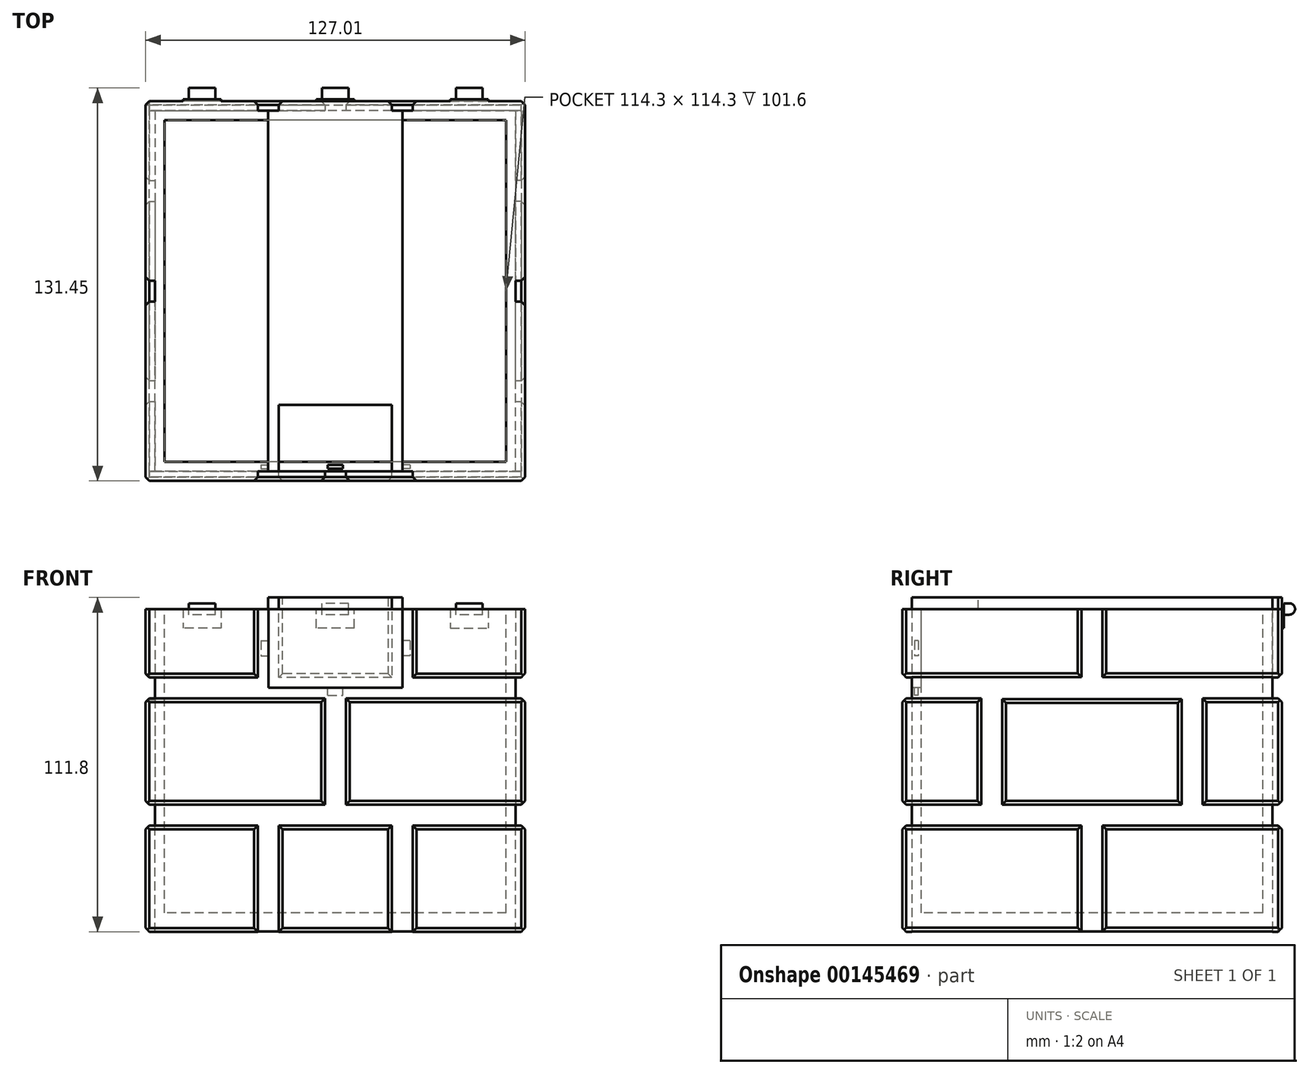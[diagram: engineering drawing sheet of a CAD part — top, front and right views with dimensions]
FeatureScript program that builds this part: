
annotation { "Feature Type Name" : "Feature", "Feature Type Description" : "" }
export const myFeature = defineFeature(function(context is Context, id is Id, definition is map)
    precondition{}
    {
        {
            var Q0;
            Q0=qCreatedBy(makeId("Front.planeOp"),FACE);
            var sketch = newSketch(context, id + "F0", { "sketchPlane" : qUnion([Q0])});
            skLineSegment(sketch, "E0.bottom", {"start": v(60.33, 60.32) * mm, "end": v(-60.33, 60.32) * mm});
            skLineSegment(sketch, "E0.top", {"start": v(60.33, -60.33) * mm, "end": v(-60.33, -60.33) * mm});
            skLineSegment(sketch, "E0.left", {"start": v(60.33, 60.32) * mm, "end": v(60.33, -60.33) * mm});
            skLineSegment(sketch, "E0.right", {"start": v(-60.32, 60.32) * mm, "end": v(-60.33, -60.33) * mm});
            skPoint(sketch, "E0.middle", {"position": v(0, 0) * mm});
            skSolve(sketch);
        }
        {
            var Q0;
            Q0=makeQuery(id+"F0.imprint","IMPRINT",FACE,{"disambiguationData":[TD([[makeQuery(id+"F0.imprint","IMPRINT",EDGE,{"derivedFrom":sQuery(id+"F0.wireOp",EDGE,"E0.bottom")}),1.0]])]});
            extrude(context, id + "F1", {"entities" : qUnion([Q0]), "depth" : 60.32 * mm, "hasSecondDirection" : true, "secondDirectionOppositeDirection" : true, "secondDirectionDepth" : 60.32 * mm});
        }
        {
            var Q0;
            Q0=makeQuery(id+"F1.opExtrude","CAP_FACE",FACE,{"disambiguationData":[OSD([sQuery(id+"F0.wireOp",EDGE,"E0.bottom"),sQuery(id+"F0.wireOp",EDGE,"E0.top"),sQuery(id+"F0.wireOp",EDGE,"E0.left"),sQuery(id+"F0.wireOp",EDGE,"E0.right")])],"isStart":false});
            var sketch = newSketch(context, id + "F2", { "sketchPlane" : qUnion([Q0])});
            skLineSegment(sketch, "E1", {"start": v(-63.5, -60.36) * mm, "end": v(-63.5, -24.8) * mm});
            skLineSegment(sketch, "E2", {"start": v(-63.5, -24.8) * mm, "end": v(-25.9, -24.8) * mm});
            skLineSegment(sketch, "E3", {"start": v(-25.9, -24.8) * mm, "end": v(-25.9, -60.36) * mm});
            skLineSegment(sketch, "E4", {"start": v(-25.9, -60.36) * mm, "end": v(-63.5, -60.36) * mm});
            skLineSegment(sketch, "E5", {"start": v(-63.5, 17.75) * mm, "end": v(-3.49, 17.75) * mm});
            skLineSegment(sketch, "E6", {"start": v(-3.49, 17.75) * mm, "end": v(-3.49, -17.81) * mm});
            skLineSegment(sketch, "E7", {"start": v(-3.49, -17.81) * mm, "end": v(-63.5, -17.81) * mm});
            skLineSegment(sketch, "E8", {"start": v(-63.5, -17.81) * mm, "end": v(-63.5, 17.75) * mm});
            skLineSegment(sketch, "E9", {"start": v(3.5, 17.75) * mm, "end": v(3.5, -17.81) * mm});
            skLineSegment(sketch, "E10", {"start": v(3.5, -17.81) * mm, "end": v(63.5, -17.81) * mm});
            skLineSegment(sketch, "E11", {"start": v(63.5, -17.81) * mm, "end": v(63.5, 17.75) * mm});
            skLineSegment(sketch, "E12", {"start": v(63.5, 17.75) * mm, "end": v(3.5, 17.75) * mm});
            skLineSegment(sketch, "E13", {"start": v(-18.92, -60.36) * mm, "end": v(-18.92, -24.8) * mm});
            skLineSegment(sketch, "E14", {"start": v(-18.92, -24.8) * mm, "end": v(18.93, -24.8) * mm});
            skLineSegment(sketch, "E15", {"start": v(18.93, -24.8) * mm, "end": v(18.93, -60.36) * mm});
            skLineSegment(sketch, "E16", {"start": v(18.93, -60.36) * mm, "end": v(-18.92, -60.36) * mm});
            skLineSegment(sketch, "E17", {"start": v(25.91, -60.36) * mm, "end": v(25.91, -24.8) * mm});
            skLineSegment(sketch, "E18", {"start": v(25.91, -24.8) * mm, "end": v(63.5, -24.8) * mm});
            skLineSegment(sketch, "E19", {"start": v(63.5, -24.8) * mm, "end": v(63.5, -60.36) * mm});
            skLineSegment(sketch, "E20", {"start": v(63.5, -60.36) * mm, "end": v(25.91, -60.36) * mm});
            skLineSegment(sketch, "E21.MirrorCS", {"start": v(-63.5, 24.73) * mm, "end": v(-25.9, 24.73) * mm});
            skLineSegment(sketch, "E22.MirrorCS", {"start": v(-25.9, 24.73) * mm, "end": v(-25.9, 60.3) * mm});
            skLineSegment(sketch, "E23.MirrorCS", {"start": v(-25.9, 60.3) * mm, "end": v(-63.5, 60.3) * mm});
            skLineSegment(sketch, "E24.MirrorCS", {"start": v(-63.5, 60.3) * mm, "end": v(-63.5, 24.73) * mm});
            skLineSegment(sketch, "E25.MirrorCS", {"start": v(-18.92, 24.73) * mm, "end": v(18.93, 24.73) * mm});
            skLineSegment(sketch, "E26.MirrorCS", {"start": v(-18.92, 60.3) * mm, "end": v(-18.92, 24.73) * mm});
            skLineSegment(sketch, "E27.MirrorCS", {"start": v(18.93, 60.3) * mm, "end": v(-18.92, 60.3) * mm});
            skLineSegment(sketch, "E28.MirrorCS", {"start": v(18.93, 24.73) * mm, "end": v(18.93, 60.3) * mm});
            skLineSegment(sketch, "E29.MirrorCS", {"start": v(25.91, 24.73) * mm, "end": v(63.5, 24.73) * mm});
            skLineSegment(sketch, "E30.MirrorCS", {"start": v(25.91, 60.3) * mm, "end": v(25.91, 24.73) * mm});
            skLineSegment(sketch, "E31.MirrorCS", {"start": v(63.5, 60.3) * mm, "end": v(25.91, 60.3) * mm});
            skLineSegment(sketch, "E32.MirrorCS", {"start": v(63.5, 24.73) * mm, "end": v(63.5, 60.3) * mm});
            skLineSegment(sketch, "E33", {"start": v(-60.32, 24.73) * mm, "end": v(-60.32, 17.75) * mm});
            skSolve(sketch);
        }
        {
            var Q0;
            Q0 = qSketchRegion(id + "F2", true);
            extrude(context, id + "F3", {"entities" : qUnion([Q0]), "operationType" : NewBodyOperationType.ADD, "depth" : 3.17 * mm});
        }
        {
            var Q0;
            Q0=makeQuery(id+"F1.opExtrude","CAP_FACE",FACE,{"disambiguationData":[OSD([sQuery(id+"F0.wireOp",EDGE,"E0.bottom"),sQuery(id+"F0.wireOp",EDGE,"E0.top"),sQuery(id+"F0.wireOp",EDGE,"E0.left"),sQuery(id+"F0.wireOp",EDGE,"E0.right")])],"isStart":true});
            var sketch = newSketch(context, id + "F4", { "sketchPlane" : qUnion([Q0])});
            skLineSegment(sketch, "E34", {"start": v(-63.5, -60.36) * mm, "end": v(-63.5, -24.8) * mm});
            skLineSegment(sketch, "E35", {"start": v(-63.5, -24.8) * mm, "end": v(-25.91, -24.8) * mm});
            skLineSegment(sketch, "E36", {"start": v(-25.91, -24.8) * mm, "end": v(-25.91, -60.36) * mm});
            skLineSegment(sketch, "E37", {"start": v(-25.91, -60.36) * mm, "end": v(-63.5, -60.36) * mm});
            skLineSegment(sketch, "E38", {"start": v(-63.5, 17.75) * mm, "end": v(-3.5, 17.75) * mm});
            skLineSegment(sketch, "E39", {"start": v(-3.5, 17.75) * mm, "end": v(-3.5, -17.81) * mm});
            skLineSegment(sketch, "E40", {"start": v(-3.5, -17.81) * mm, "end": v(-63.5, -17.81) * mm});
            skLineSegment(sketch, "E41", {"start": v(-63.5, -17.81) * mm, "end": v(-63.5, 17.75) * mm});
            skLineSegment(sketch, "E42", {"start": v(3.49, 17.75) * mm, "end": v(3.49, -17.81) * mm});
            skLineSegment(sketch, "E43", {"start": v(3.49, -17.81) * mm, "end": v(63.5, -17.81) * mm});
            skLineSegment(sketch, "E44", {"start": v(63.5, -17.81) * mm, "end": v(63.5, 17.75) * mm});
            skLineSegment(sketch, "E45", {"start": v(63.5, 17.75) * mm, "end": v(3.49, 17.75) * mm});
            skLineSegment(sketch, "E46", {"start": v(-18.93, -60.36) * mm, "end": v(-18.93, -24.8) * mm});
            skLineSegment(sketch, "E47", {"start": v(-18.93, -24.8) * mm, "end": v(18.92, -24.8) * mm});
            skLineSegment(sketch, "E48", {"start": v(18.92, -24.8) * mm, "end": v(18.92, -60.36) * mm});
            skLineSegment(sketch, "E49", {"start": v(18.92, -60.36) * mm, "end": v(-18.93, -60.36) * mm});
            skLineSegment(sketch, "E50", {"start": v(25.9, -60.36) * mm, "end": v(25.9, -24.8) * mm});
            skLineSegment(sketch, "E51", {"start": v(25.9, -24.8) * mm, "end": v(63.5, -24.8) * mm});
            skLineSegment(sketch, "E52", {"start": v(63.5, -24.8) * mm, "end": v(63.5, -60.36) * mm});
            skLineSegment(sketch, "E53", {"start": v(63.5, -60.36) * mm, "end": v(25.9, -60.36) * mm});
            skLineSegment(sketch, "E54.MirrorCS", {"start": v(-63.5, 24.73) * mm, "end": v(-25.91, 24.73) * mm});
            skLineSegment(sketch, "E55.MirrorCS", {"start": v(-25.91, 24.73) * mm, "end": v(-25.91, 60.3) * mm});
            skLineSegment(sketch, "E56.MirrorCS", {"start": v(-25.91, 60.3) * mm, "end": v(-63.5, 60.3) * mm});
            skLineSegment(sketch, "E57.MirrorCS", {"start": v(-63.5, 60.3) * mm, "end": v(-63.5, 24.73) * mm});
            skLineSegment(sketch, "E58.MirrorCS", {"start": v(-18.93, 24.73) * mm, "end": v(18.92, 24.73) * mm});
            skLineSegment(sketch, "E59.MirrorCS", {"start": v(-18.93, 60.3) * mm, "end": v(-18.93, 24.73) * mm});
            skLineSegment(sketch, "E60.MirrorCS", {"start": v(18.92, 60.3) * mm, "end": v(-18.93, 60.3) * mm});
            skLineSegment(sketch, "E61.MirrorCS", {"start": v(18.92, 24.73) * mm, "end": v(18.92, 60.3) * mm});
            skLineSegment(sketch, "E62.MirrorCS", {"start": v(25.9, 24.73) * mm, "end": v(63.5, 24.73) * mm});
            skLineSegment(sketch, "E63.MirrorCS", {"start": v(25.9, 60.3) * mm, "end": v(25.9, 24.73) * mm});
            skLineSegment(sketch, "E64.MirrorCS", {"start": v(63.5, 60.3) * mm, "end": v(25.9, 60.3) * mm});
            skLineSegment(sketch, "E65.MirrorCS", {"start": v(63.5, 24.73) * mm, "end": v(63.5, 60.3) * mm});
            skLineSegment(sketch, "E66", {"start": v(-60.33, 24.73) * mm, "end": v(-60.33, 17.75) * mm});
            skSolve(sketch);
        }
        {
            var Q0;
            {var subQ0=sQuery(id+"F4.wireOp",EDGE,"E55.MirrorCS");Q0=makeQuery(id+"F4.imprint","IMPRINT",FACE,{"disambiguationData":[TD([[makeQuery(id+"F4.imprint","IMPRINT",EDGE,{"derivedFrom":subQ0}),1.0]])]});}
            var Q1;
            Q1=makeQuery(id+"F4.imprint","IMPRINT",FACE,{"disambiguationData":[TD([[makeQuery(id+"F4.imprint","IMPRINT",EDGE,{"derivedFrom":sQuery(id+"F4.wireOp",EDGE,"E59.MirrorCS")}),1.0]])]});
            var Q2;
            {var subQ0=sQuery(id+"F4.wireOp",EDGE,"E39");Q2=makeQuery(id+"F4.imprint","IMPRINT",FACE,{"disambiguationData":[TD([[makeQuery(id+"F4.imprint","IMPRINT",EDGE,{"derivedFrom":subQ0}),-1.0]])]});}
            var Q3;
            {var subQ0=sQuery(id+"F4.wireOp",EDGE,"E41");Q3=makeQuery(id+"F4.imprint","IMPRINT",FACE,{"disambiguationData":[TD([[makeQuery(id+"F4.imprint","IMPRINT",EDGE,{"derivedFrom":subQ0}),-1.0]])]});}
            var Q4;
            {var subQ0=sQuery(id+"F4.wireOp",EDGE,"E57.MirrorCS");Q4=makeQuery(id+"F4.imprint","IMPRINT",FACE,{"disambiguationData":[TD([[makeQuery(id+"F4.imprint","IMPRINT",EDGE,{"derivedFrom":subQ0}),1.0]])]});}
            var Q5;
            {var subQ0=sQuery(id+"F4.wireOp",EDGE,"E63.MirrorCS");Q5=makeQuery(id+"F4.imprint","IMPRINT",FACE,{"disambiguationData":[TD([[makeQuery(id+"F4.imprint","IMPRINT",EDGE,{"derivedFrom":subQ0}),1.0]])]});}
            var Q6;
            {var subQ0=sQuery(id+"F4.wireOp",EDGE,"E65.MirrorCS");Q6=makeQuery(id+"F4.imprint","IMPRINT",FACE,{"disambiguationData":[TD([[makeQuery(id+"F4.imprint","IMPRINT",EDGE,{"derivedFrom":subQ0}),1.0]])]});}
            var Q7;
            {var subQ0=sQuery(id+"F4.wireOp",EDGE,"E42");Q7=makeQuery(id+"F4.imprint","IMPRINT",FACE,{"disambiguationData":[TD([[makeQuery(id+"F4.imprint","IMPRINT",EDGE,{"derivedFrom":subQ0}),1.0]])]});}
            var Q8;
            {var subQ0=sQuery(id+"F4.wireOp",EDGE,"E44");Q8=makeQuery(id+"F4.imprint","IMPRINT",FACE,{"disambiguationData":[TD([[makeQuery(id+"F4.imprint","IMPRINT",EDGE,{"derivedFrom":subQ0}),1.0]])]});}
            var Q9;
            {var subQ6=sQuery(id+"F4.wireOp",EDGE,"E52");Q9=makeQuery(id+"F4.imprint","IMPRINT",FACE,{"disambiguationData":[TD([[makeQuery(id+"F4.imprint","IMPRINT",EDGE,{"derivedFrom":subQ6}),-1.0]])]});}
            var Q10;
            {var subQ0=sQuery(id+"F4.wireOp",EDGE,"E51");var subQ1=sQuery(id+"F4.wireOp",EDGE,"E50");var subQ2=makeQuery(id+"F4.imprint","INTERSECT",VERTEX,{"derivedFrom":[subQ1,subQ0]});Q10=makeQuery(id+"F4.imprint","IMPRINT",FACE,{"disambiguationData":[TD([[makeQuery(id+"F4.imprint","IMPRINT",EDGE,{"disambiguationData":[TD([[subQ2,1.0]])],"derivedFrom":subQ1}),-1.0]])]});}
            var Q11;
            {var subQ0=sQuery(id+"F4.wireOp",EDGE,"E47");Q11=makeQuery(id+"F4.imprint","IMPRINT",FACE,{"disambiguationData":[TD([[makeQuery(id+"F4.imprint","IMPRINT",EDGE,{"derivedFrom":subQ0}),-1.0]])]});}
            var Q12;
            {var subQ0=sQuery(id+"F4.wireOp",EDGE,"E36");var subQ1=sQuery(id+"F4.wireOp",EDGE,"E35");var subQ2=makeQuery(id+"F4.imprint","INTERSECT",VERTEX,{"derivedFrom":[subQ1,subQ0]});Q12=makeQuery(id+"F4.imprint","IMPRINT",FACE,{"disambiguationData":[TD([[makeQuery(id+"F4.imprint","IMPRINT",EDGE,{"disambiguationData":[TD([[subQ2,1.0]])],"derivedFrom":subQ1}),-1.0]])]});}
            var Q13;
            {var subQ2=sQuery(id+"F4.wireOp",EDGE,"E34");Q13=makeQuery(id+"F4.imprint","IMPRINT",FACE,{"disambiguationData":[TD([[makeQuery(id+"F4.imprint","IMPRINT",EDGE,{"derivedFrom":subQ2}),-1.0]])]});}
            extrude(context, id + "F5", {"entities" : qUnion([Q0, Q1, Q2, Q3, Q4, Q5, Q6, Q7, Q8, Q9, Q10, Q11, Q12, Q13]), "operationType" : NewBodyOperationType.ADD, "depth" : 3.17 * mm});
        }
        {
            var Q0;
            Q0=makeQuery(id+"F1.opExtrude","SWEPT_FACE",FACE,{"disambiguationData":[OSD([sQuery(id+"F0.wireOp",EDGE,"E0.left")])]});
            var sketch = newSketch(context, id + "F6", { "sketchPlane" : qUnion([Q0])});
            skLineSegment(sketch, "E67.bottom", {"start": v(-63.5, 60.33) * mm, "end": v(-3.5, 60.33) * mm});
            skLineSegment(sketch, "E67.top", {"start": v(-63.5, 24.77) * mm, "end": v(-3.5, 24.77) * mm});
            skLineSegment(sketch, "E67.left", {"start": v(-63.5, 60.33) * mm, "end": v(-63.5, 24.77) * mm});
            skLineSegment(sketch, "E67.right", {"start": v(-3.5, 60.33) * mm, "end": v(-3.5, 24.77) * mm});
            skLineSegment(sketch, "E68.bottom", {"start": v(63.5, 60.33) * mm, "end": v(3.5, 60.33) * mm});
            skLineSegment(sketch, "E68.top", {"start": v(63.5, 24.76) * mm, "end": v(3.5, 24.76) * mm});
            skLineSegment(sketch, "E68.left", {"start": v(63.5, 60.33) * mm, "end": v(63.5, 24.76) * mm});
            skLineSegment(sketch, "E68.right", {"start": v(3.5, 60.33) * mm, "end": v(3.5, 24.76) * mm});
            skLineSegment(sketch, "E69.bottom", {"start": v(-63.5, 17.75) * mm, "end": v(-37, 17.75) * mm});
            skLineSegment(sketch, "E69.top", {"start": v(-63.5, -17.81) * mm, "end": v(-37, -17.81) * mm});
            skLineSegment(sketch, "E69.left", {"start": v(-63.5, 17.75) * mm, "end": v(-63.5, -17.81) * mm});
            skLineSegment(sketch, "E69.right", {"start": v(-37, 17.75) * mm, "end": v(-37, -17.81) * mm});
            skLineSegment(sketch, "E70.bottom", {"start": v(-30.01, 17.38) * mm, "end": v(30, 17.38) * mm});
            skLineSegment(sketch, "E70.top", {"start": v(-30.01, -17.81) * mm, "end": v(30, -17.81) * mm});
            skLineSegment(sketch, "E70.left", {"start": v(-30.01, 17.38) * mm, "end": v(-30.01, -17.81) * mm});
            skLineSegment(sketch, "E70.right", {"start": v(30, 17.38) * mm, "end": v(30, -17.81) * mm});
            skLineSegment(sketch, "E71.bottom", {"start": v(36.98, 17.75) * mm, "end": v(63.49, 17.75) * mm});
            skLineSegment(sketch, "E71.top", {"start": v(36.98, -17.81) * mm, "end": v(63.49, -17.81) * mm});
            skLineSegment(sketch, "E71.left", {"start": v(36.98, 17.75) * mm, "end": v(36.98, -17.81) * mm});
            skLineSegment(sketch, "E71.right", {"start": v(63.49, 17.75) * mm, "end": v(63.49, -17.81) * mm});
            skLineSegment(sketch, "E72.bottom", {"start": v(-63.5, -60.33) * mm, "end": v(-3.5, -60.33) * mm});
            skLineSegment(sketch, "E72.top", {"start": v(-63.5, -24.8) * mm, "end": v(-3.5, -24.8) * mm});
            skLineSegment(sketch, "E72.left", {"start": v(-63.5, -60.33) * mm, "end": v(-63.5, -24.8) * mm});
            skLineSegment(sketch, "E72.right", {"start": v(-3.5, -60.33) * mm, "end": v(-3.5, -24.8) * mm});
            skLineSegment(sketch, "E73.bottom", {"start": v(63.5, -60.33) * mm, "end": v(3.5, -60.33) * mm});
            skLineSegment(sketch, "E73.top", {"start": v(63.5, -24.8) * mm, "end": v(3.5, -24.8) * mm});
            skLineSegment(sketch, "E73.left", {"start": v(63.5, -60.33) * mm, "end": v(63.5, -24.8) * mm});
            skLineSegment(sketch, "E73.right", {"start": v(3.5, -60.33) * mm, "end": v(3.5, -24.8) * mm});
            skSolve(sketch);
        }
        {
            var Q0;
            {var subQ10=sQuery(id+"F6.wireOp",EDGE,"E68.right");Q0=makeQuery(id+"F6.imprint","IMPRINT",FACE,{"disambiguationData":[TD([[makeQuery(id+"F6.imprint","IMPRINT",EDGE,{"derivedFrom":subQ10}),1.0]])]});}
            var Q1;
            Q1=makeQuery(id+"F6.imprint","IMPRINT",FACE,{"disambiguationData":[TD([[makeQuery(id+"F6.imprint","IMPRINT",EDGE,{"derivedFrom":sQuery(id+"F6.wireOp",EDGE,"E70.bottom")}),-1.0]])]});
            var Q2;
            {var subQ14=sQuery(id+"F6.wireOp",EDGE,"E71.left");Q2=makeQuery(id+"F6.imprint","IMPRINT",FACE,{"disambiguationData":[TD([[makeQuery(id+"F6.imprint","IMPRINT",EDGE,{"derivedFrom":subQ14}),1.0]])]});}
            var Q3;
            {var subQ12=sQuery(id+"F6.wireOp",EDGE,"E69.right");Q3=makeQuery(id+"F6.imprint","IMPRINT",FACE,{"disambiguationData":[TD([[makeQuery(id+"F6.imprint","IMPRINT",EDGE,{"derivedFrom":subQ12}),-1.0]])]});}
            var Q4;
            {var subQ10=sQuery(id+"F6.wireOp",EDGE,"E72.right");Q4=makeQuery(id+"F6.imprint","IMPRINT",FACE,{"disambiguationData":[TD([[makeQuery(id+"F6.imprint","IMPRINT",EDGE,{"derivedFrom":subQ10}),1.0]])]});}
            var Q5;
            {var subQ6=sQuery(id+"F6.wireOp",EDGE,"E73.right");Q5=makeQuery(id+"F6.imprint","IMPRINT",FACE,{"disambiguationData":[TD([[makeQuery(id+"F6.imprint","IMPRINT",EDGE,{"derivedFrom":subQ6}),-1.0]])]});}
            var Q6;
            {var subQ10=sQuery(id+"F6.wireOp",EDGE,"E67.right");Q6=makeQuery(id+"F6.imprint","IMPRINT",FACE,{"disambiguationData":[TD([[makeQuery(id+"F6.imprint","IMPRINT",EDGE,{"derivedFrom":subQ10}),-1.0]])]});}
            extrude(context, id + "F7", {"entities" : qUnion([Q0, Q1, Q2, Q3, Q4, Q5, Q6]), "operationType" : NewBodyOperationType.ADD, "depth" : 3.17 * mm});
        }
        {
            var Q0;
            Q0=makeQuery(id+"F1.opExtrude","SWEPT_FACE",FACE,{"disambiguationData":[OSD([sQuery(id+"F0.wireOp",EDGE,"E0.right")])]});
            var sketch = newSketch(context, id + "F8", { "sketchPlane" : qUnion([Q0])});
            skLineSegment(sketch, "E74.bottom", {"start": v(-63.5, 60.3) * mm, "end": v(-3.5, 60.3) * mm});
            skLineSegment(sketch, "E74.top", {"start": v(-63.5, 24.73) * mm, "end": v(-3.5, 24.73) * mm});
            skLineSegment(sketch, "E74.left", {"start": v(-63.5, 60.3) * mm, "end": v(-63.5, 24.73) * mm});
            skLineSegment(sketch, "E74.right", {"start": v(-3.5, 60.3) * mm, "end": v(-3.5, 24.73) * mm});
            skLineSegment(sketch, "E75.bottom", {"start": v(63.5, 60.3) * mm, "end": v(3.5, 60.3) * mm});
            skLineSegment(sketch, "E75.top", {"start": v(63.5, 24.73) * mm, "end": v(3.5, 24.73) * mm});
            skLineSegment(sketch, "E75.left", {"start": v(63.5, 60.3) * mm, "end": v(63.5, 24.73) * mm});
            skLineSegment(sketch, "E75.right", {"start": v(3.5, 60.3) * mm, "end": v(3.5, 24.73) * mm});
            skLineSegment(sketch, "E76.bottom", {"start": v(-63.5, 17.72) * mm, "end": v(-37, 17.72) * mm});
            skLineSegment(sketch, "E76.top", {"start": v(-63.5, -17.84) * mm, "end": v(-37, -17.84) * mm});
            skLineSegment(sketch, "E76.left", {"start": v(-63.5, 17.72) * mm, "end": v(-63.5, -17.84) * mm});
            skLineSegment(sketch, "E76.right", {"start": v(-37, 17.72) * mm, "end": v(-37, -17.84) * mm});
            skLineSegment(sketch, "E77.bottom", {"start": v(-30, 17.35) * mm, "end": v(30, 17.35) * mm});
            skLineSegment(sketch, "E77.top", {"start": v(-30, -17.84) * mm, "end": v(30, -17.84) * mm});
            skLineSegment(sketch, "E77.left", {"start": v(-30, 17.35) * mm, "end": v(-30, -17.84) * mm});
            skLineSegment(sketch, "E77.right", {"start": v(30, 17.35) * mm, "end": v(30, -17.84) * mm});
            skLineSegment(sketch, "E78.bottom", {"start": v(36.98, 17.72) * mm, "end": v(63.49, 17.72) * mm});
            skLineSegment(sketch, "E78.top", {"start": v(36.98, -17.84) * mm, "end": v(63.49, -17.84) * mm});
            skLineSegment(sketch, "E78.left", {"start": v(36.98, 17.72) * mm, "end": v(36.98, -17.84) * mm});
            skLineSegment(sketch, "E78.right", {"start": v(63.49, 17.72) * mm, "end": v(63.49, -17.84) * mm});
            skLineSegment(sketch, "E79.bottom", {"start": v(-63.5, -60.36) * mm, "end": v(-3.5, -60.36) * mm});
            skLineSegment(sketch, "E79.top", {"start": v(-63.5, -24.83) * mm, "end": v(-3.5, -24.83) * mm});
            skLineSegment(sketch, "E79.left", {"start": v(-63.5, -60.36) * mm, "end": v(-63.5, -24.83) * mm});
            skLineSegment(sketch, "E79.right", {"start": v(-3.5, -60.36) * mm, "end": v(-3.5, -24.83) * mm});
            skLineSegment(sketch, "E80.bottom", {"start": v(63.5, -60.36) * mm, "end": v(3.5, -60.36) * mm});
            skLineSegment(sketch, "E80.top", {"start": v(63.5, -24.83) * mm, "end": v(3.5, -24.83) * mm});
            skLineSegment(sketch, "E80.left", {"start": v(63.5, -60.36) * mm, "end": v(63.5, -24.83) * mm});
            skLineSegment(sketch, "E80.right", {"start": v(3.5, -60.36) * mm, "end": v(3.5, -24.83) * mm});
            skSolve(sketch);
        }
        {
            var Q0;
            {var subQ14=sQuery(id+"F8.wireOp",EDGE,"E74.right");Q0=makeQuery(id+"F8.imprint","IMPRINT",FACE,{"disambiguationData":[TD([[makeQuery(id+"F8.imprint","IMPRINT",EDGE,{"derivedFrom":subQ14}),-1.0]])]});}
            var Q1;
            {var subQ12=sQuery(id+"F8.wireOp",EDGE,"E75.right");Q1=makeQuery(id+"F8.imprint","IMPRINT",FACE,{"disambiguationData":[TD([[makeQuery(id+"F8.imprint","IMPRINT",EDGE,{"derivedFrom":subQ12}),1.0]])]});}
            var Q2;
            {var subQ0=sQuery(id+"F8.wireOp",EDGE,"E78.left");Q2=makeQuery(id+"F8.imprint","IMPRINT",FACE,{"disambiguationData":[TD([[makeQuery(id+"F8.imprint","IMPRINT",EDGE,{"derivedFrom":subQ0}),1.0]])]});}
            var Q3;
            Q3=makeQuery(id+"F8.imprint","IMPRINT",FACE,{"disambiguationData":[TD([[makeQuery(id+"F8.imprint","IMPRINT",EDGE,{"derivedFrom":sQuery(id+"F8.wireOp",EDGE,"E77.bottom")}),-1.0]])]});
            var Q4;
            {var subQ14=sQuery(id+"F8.wireOp",EDGE,"E76.right");Q4=makeQuery(id+"F8.imprint","IMPRINT",FACE,{"disambiguationData":[TD([[makeQuery(id+"F8.imprint","IMPRINT",EDGE,{"derivedFrom":subQ14}),-1.0]])]});}
            var Q5;
            {var subQ0=sQuery(id+"F8.wireOp",EDGE,"E79.right");var subQ1=sQuery(id+"F8.wireOp",EDGE,"E79.top");var subQ2=makeQuery(id+"F8.imprint","INTERSECT",VERTEX,{"derivedFrom":[subQ1,subQ0]});Q5=makeQuery(id+"F8.imprint","IMPRINT",FACE,{"disambiguationData":[TD([[makeQuery(id+"F8.imprint","IMPRINT",EDGE,{"disambiguationData":[TD([[subQ2,1.0]])],"derivedFrom":subQ0}),1.0]])]});}
            var Q6;
            {var subQ0=sQuery(id+"F8.wireOp",EDGE,"E80.right");var subQ1=sQuery(id+"F8.wireOp",EDGE,"E80.top");var subQ2=makeQuery(id+"F8.imprint","INTERSECT",VERTEX,{"derivedFrom":[subQ1,subQ0]});Q6=makeQuery(id+"F8.imprint","IMPRINT",FACE,{"disambiguationData":[TD([[makeQuery(id+"F8.imprint","IMPRINT",EDGE,{"disambiguationData":[TD([[subQ2,1.0]])],"derivedFrom":subQ0}),-1.0]])]});}
            extrude(context, id + "F9", {"entities" : qUnion([Q0, Q1, Q2, Q3, Q4, Q5, Q6]), "operationType" : NewBodyOperationType.ADD, "depth" : 3.17 * mm});
        }
        {
            var Q0;
            Q0=makeQuery(id+"F7.boolean.opBoolean","MERGE",FACE,{"derivedFrom":[makeQuery(id+"F1.opExtrude","SWEPT_FACE",FACE,{"disambiguationData":[OSD([sQuery(id+"F0.wireOp",EDGE,"E0.bottom")])]}),makeQuery(id+"F7.opExtrude","SWEPT_FACE",FACE,{"disambiguationData":[OSD([sQuery(id+"F6.wireOp",EDGE,"E67.bottom")])]}),makeQuery(id+"F7.opExtrude","SWEPT_FACE",FACE,{"disambiguationData":[OSD([sQuery(id+"F6.wireOp",EDGE,"E68.bottom")])]})]});
            var sketch = newSketch(context, id + "F10", { "sketchPlane" : qUnion([Q0])});
            skLineSegment(sketch, "E81", {"start": v(-25.9, 63.5) * mm, "end": v(-25.9, -63.5) * mm});
            skLineSegment(sketch, "E82", {"start": v(-18.92, 63.49) * mm, "end": v(-18.92, -63.5) * mm});
            skLineSegment(sketch, "E83", {"start": v(18.93, 63.5) * mm, "end": v(18.93, -63.5) * mm});
            skLineSegment(sketch, "E84", {"start": v(25.91, 63.5) * mm, "end": v(25.91, -63.5) * mm});
            skLineSegment(sketch, "E85", {"start": v(-63.5, 3.5) * mm, "end": v(63.5, 3.5) * mm});
            skLineSegment(sketch, "E86", {"start": v(63.5, -3.5) * mm, "end": v(-63.5, -3.5) * mm});
            skLineSegment(sketch, "E87", {"start": v(-18.92, 36.98) * mm, "end": v(18.93, 36.98) * mm});
            skLineSegment(sketch, "E88", {"start": v(-18.92, -37) * mm, "end": v(18.93, -37) * mm});
            skLineSegment(sketch, "E89", {"start": v(-18.92, 30) * mm, "end": v(18.93, 30) * mm});
            skLineSegment(sketch, "E90", {"start": v(-18.92, -30.01) * mm, "end": v(18.93, -30.01) * mm});
            skSolve(sketch);
        }
        {
            var Q0;
            Q0=makeQuery(id+"F3.opExtrude","CAP_FACE",FACE,{"disambiguationData":[OSD([sQuery(id+"F2.wireOp",EDGE,"E21.MirrorCS"),sQuery(id+"F2.wireOp",EDGE,"E22.MirrorCS"),sQuery(id+"F2.wireOp",EDGE,"E23.MirrorCS"),sQuery(id+"F2.wireOp",EDGE,"E24.MirrorCS")])],"isStart":false});
            var sketch = newSketch(context, id + "F11", { "sketchPlane" : qUnion([Q0])});
            skLineSegment(sketch, "E91.bottom", {"start": v(-63.5, 60.3) * mm, "end": v(63.5, 60.3) * mm});
            skLineSegment(sketch, "E91.top", {"start": v(-63.5, 47.6) * mm, "end": v(63.5, 47.6) * mm});
            skLineSegment(sketch, "E91.left", {"start": v(-63.5, 60.3) * mm, "end": v(-63.5, 47.6) * mm});
            skLineSegment(sketch, "E91.right", {"start": v(63.5, 60.3) * mm, "end": v(63.5, 47.6) * mm});
            skLineSegment(sketch, "E92.bottom", {"start": v(-22.49, 60.3) * mm, "end": v(22.5, 60.3) * mm});
            skLineSegment(sketch, "E92.top", {"start": v(-22.49, 21.12) * mm, "end": v(22.5, 21.12) * mm});
            skLineSegment(sketch, "E92.left", {"start": v(-22.49, 60.3) * mm, "end": v(-22.49, 21.12) * mm});
            skLineSegment(sketch, "E92.right", {"start": v(22.5, 60.3) * mm, "end": v(22.5, 21.12) * mm});
            skLineSegment(sketch, "E93", {"start": v(-22.49, 60.3) * mm, "end": v(-63.5, 60.3) * mm});
            skLineSegment(sketch, "E94", {"start": v(22.5, 60.3) * mm, "end": v(63.5, 60.3) * mm});
            skSolve(sketch);
        }
        {
            var Q0;
            {var subQ0=sQuery(id+"F11.wireOp",EDGE,"E91.left");Q0=makeQuery(id+"F11.imprint","IMPRINT",FACE,{"disambiguationData":[TD([[makeQuery(id+"F11.imprint","IMPRINT",EDGE,{"derivedFrom":subQ0}),1.0]])]});}
            var Q1;
            {var subQ0=sQuery(id+"F11.wireOp",EDGE,"E92.left");var subQ1=sQuery(id+"F11.wireOp",EDGE,"E91.top");var subQ2=makeQuery(id+"F11.imprint","INTERSECT",VERTEX,{"derivedFrom":[subQ1,subQ0]});Q1=makeQuery(id+"F11.imprint","IMPRINT",FACE,{"disambiguationData":[TD([[makeQuery(id+"F11.imprint","IMPRINT",EDGE,{"disambiguationData":[TD([[subQ2,1.0]])],"derivedFrom":subQ1}),1.0]])]});}
            var Q2;
            {var subQ5=sQuery(id+"F11.wireOp",EDGE,"E92.bottom");Q2=makeQuery(id+"F11.imprint","IMPRINT",FACE,{"disambiguationData":[TD([[makeQuery(id+"F11.imprint","IMPRINT",EDGE,{"derivedFrom":subQ5}),-1.0]])]});}
            var Q3;
            {var subQ0=sQuery(id+"F11.wireOp",EDGE,"E91.right");Q3=makeQuery(id+"F11.imprint","IMPRINT",FACE,{"disambiguationData":[TD([[makeQuery(id+"F11.imprint","IMPRINT",EDGE,{"derivedFrom":subQ0}),-1.0]])]});}
            extrude(context, id + "F12", {"entities" : qUnion([Q0, Q1, Q2, Q3]), "operationType" : NewBodyOperationType.REMOVE, "oppositeDirection" : true, "depth" : 127 * mm});
        }
        {
            var Q0;
            {var subQ0=sQuery(id+"F10.wireOp",EDGE,"E85");var subQ1=sQuery(id+"F10.wireOp",EDGE,"E81");var subQ2=makeQuery(id+"F10.imprint","INTERSECT",VERTEX,{"derivedFrom":[subQ1,subQ0]});Q0=makeQuery(id+"F10.imprint","IMPRINT",FACE,{"disambiguationData":[TD([[makeQuery(id+"F10.imprint","IMPRINT",EDGE,{"disambiguationData":[TD([[subQ2,1.0]])],"derivedFrom":subQ0}),1.0]])]});}
            var sketch = newSketch(context, id + "F13", { "sketchPlane" : qUnion([Q0])});
            skLineSegment(sketch, "E95.bottom", {"start": v(-81.28, 79.88) * mm, "end": v(97.75, 79.88) * mm});
            skLineSegment(sketch, "E95.top", {"start": v(-81.28, -89.36) * mm, "end": v(97.75, -89.36) * mm});
            skLineSegment(sketch, "E95.left", {"start": v(-81.28, 79.88) * mm, "end": v(-81.28, -89.36) * mm});
            skLineSegment(sketch, "E95.right", {"start": v(97.75, 79.88) * mm, "end": v(97.75, -89.36) * mm});
            skSolve(sketch);
        }
        {
            var Q0;
            Q0 = qSketchRegion(id + "F13", true);
            extrude(context, id + "F14", {"entities" : qUnion([Q0]), "operationType" : NewBodyOperationType.REMOVE, "oppositeDirection" : true, "depth" : 8.9 * mm});
        }
        {
            var Q0;
            Q0=makeQuery(id+"F12.boolean.opBoolean","COPY",FACE,{"derivedFrom":makeQuery(id+"F12.opExtrude","SWEPT_FACE",FACE,{"disambiguationData":[OSD([sQuery(id+"F11.wireOp",EDGE,"E91.top")])]})});
            var sketch = newSketch(context, id + "F15", { "sketchPlane" : qUnion([Q0])});
            skLineSegment(sketch, "E96.bottom", {"start": v(57.15, 57.15) * mm, "end": v(-57.15, 57.15) * mm});
            skLineSegment(sketch, "E96.top", {"start": v(57.15, -57.15) * mm, "end": v(-57.15, -57.15) * mm});
            skLineSegment(sketch, "E96.left", {"start": v(57.15, 57.15) * mm, "end": v(57.15, -57.15) * mm});
            skLineSegment(sketch, "E96.right", {"start": v(-57.15, 57.15) * mm, "end": v(-57.15, -57.15) * mm});
            skPoint(sketch, "E96.middle", {"position": v(0, 0) * mm});
            skSolve(sketch);
        }
        {
            var Q0;
            Q0=makeQuery(id+"F15.imprint","IMPRINT",FACE,{"disambiguationData":[TD([[makeQuery(id+"F15.imprint","IMPRINT",EDGE,{"derivedFrom":sQuery(id+"F15.wireOp",EDGE,"E96.bottom")}),1.0]])]});
            extrude(context, id + "F16", {"entities" : qUnion([Q0]), "operationType" : NewBodyOperationType.REMOVE, "oppositeDirection" : true, "depth" : 101.6 * mm});
        }
        {
            var Q0;
            {var subQ4=sQuery(id+"F0.wireOp",EDGE,"E0.left");var subQ5=makeQuery(id+"F1.opExtrude","SWEPT_FACE",FACE,{"disambiguationData":[OSD([subQ4])]});var subQ7=sQuery(id+"F0.wireOp",EDGE,"E0.right");var subQ8=makeQuery(id+"F1.opExtrude","SWEPT_FACE",FACE,{"disambiguationData":[OSD([subQ7])]});var subQ9=sQuery(id+"F0.wireOp",EDGE,"E0.top");var subQ11=makeQuery(id+"F1.opExtrude","SWEPT_FACE",FACE,{"disambiguationData":[OSD([subQ9])]});var subQ12=sQuery(id+"F0.wireOp",EDGE,"E0.bottom");var subQ14=sQuery(id+"F2.wireOp",EDGE,"E8");var subQ15=sQuery(id+"F2.wireOp",EDGE,"E7");var subQ16=sQuery(id+"F2.wireOp",EDGE,"E6");var subQ17=sQuery(id+"F2.wireOp",EDGE,"E5");var subQ18=makeQuery(id+"F3.opExtrude","CAP_FACE",FACE,{"disambiguationData":[OSD([subQ17,subQ16,subQ15,subQ14])],"isStart":true});var subQ19=sQuery(id+"F2.wireOp",EDGE,"E3");var subQ20=sQuery(id+"F2.wireOp",EDGE,"E2");var subQ21=makeQuery(id+"F3.opExtrude","CAP_FACE",FACE,{"disambiguationData":[OSD([sQuery(id+"F2.wireOp",EDGE,"E1"),subQ20,subQ19,sQuery(id+"F2.wireOp",EDGE,"E4")])],"isStart":true});var subQ22=makeQuery(id+"F3.opExtrude","SWEPT_FACE",FACE,{"disambiguationData":[OSD([subQ20])]});var subQ24=makeQuery(id+"F3.opExtrude","SWEPT_FACE",FACE,{"disambiguationData":[OSD([subQ17])]});var subQ25=makeQuery(id+"F3.opExtrude","SWEPT_FACE",FACE,{"disambiguationData":[OSD([subQ15])]});var subQ26=makeQuery(id+"F1.opExtrude","CAP_FACE",FACE,{"disambiguationData":[OSD([subQ12,subQ9,subQ4,subQ7])],"isStart":false});var subQ27=makeQuery(id+"F1.opExtrude","CAP_EDGE",EDGE,{"disambiguationData":[OSD([subQ7])],"isStart":false});var subQ28=sQuery(id+"F8.wireOp",EDGE,"E78.top");var subQ29=sQuery(id+"F2.wireOp",EDGE,"E29.MirrorCS");var subQ30=makeQuery(id+"F3.opExtrude","SWEPT_FACE",FACE,{"disambiguationData":[OSD([subQ29])]});var subQ31=sQuery(id+"F2.wireOp",EDGE,"E31.MirrorCS");var subQ32=sQuery(id+"F2.wireOp",EDGE,"E30.MirrorCS");var subQ33=makeQuery(id+"F3.opExtrude","CAP_FACE",FACE,{"disambiguationData":[OSD([subQ29,subQ32,subQ31,sQuery(id+"F2.wireOp",EDGE,"E32.MirrorCS")])],"isStart":true});var subQ34=sQuery(id+"F8.wireOp",EDGE,"E78.bottom");var subQ35=makeQuery(id+"F3.boolean.opBoolean","SPLIT",EDGE,{"disambiguationData":[TD([subQ26,subQ8,subQ21,subQ22,subQ18,subQ25])],"derivedFrom":subQ27});var subQ36=makeQuery(id+"F3.boolean.opBoolean","SPLIT",EDGE,{"disambiguationData":[TD([subQ26,subQ8,subQ24,subQ18,subQ25])],"derivedFrom":subQ27});var subQ38=makeQuery(id+"F3.opExtrude","SWEPT_FACE",FACE,{"disambiguationData":[OSD([subQ31])]});var subQ39=makeQuery(id+"F1.opExtrude","CAP_EDGE",EDGE,{"disambiguationData":[OSD([subQ4])],"isStart":false});var subQ40=makeQuery(id+"F3.boolean.opBoolean","SPLIT",EDGE,{"disambiguationData":[TD([subQ26,subQ5,subQ30,subQ33,subQ38])],"derivedFrom":subQ39});var subQ41=makeQuery(id+"F3.boolean.opBoolean","SPLIT",EDGE,{"disambiguationData":[TD([makeQuery(id+"F1.opExtrude","SWEPT_FACE",FACE,{"disambiguationData":[OSD([subQ12])]}),subQ26,subQ5,subQ33,subQ38])],"derivedFrom":subQ39});Q0=makeQuery(id+"F12.boolean.opBoolean","SPLIT",FACE,{"disambiguationData":[TD([subQ11])],"derivedFrom":makeQuery(id+"F9.boolean.opBoolean","MERGE",FACE,{"derivedFrom":[makeQuery(id+"F7.boolean.opBoolean","MERGE",FACE,{"derivedFrom":[subQ26,makeQuery(id+"F7.opExtrude","SWEPT_FACE",FACE,{"disambiguationData":[OSD([subQ4]),TDD([makeQuery(id+"F6.imprint","IMPRINT",EDGE,{"derivedFrom":subQ41}),makeQuery(id+"F6.imprint","IMPRINT",EDGE,{"disambiguationData":[TD([[makeQuery(id+"F6.imprint","INTERSECT",VERTEX,{"derivedFrom":[subQ40,sQuery(id+"F6.wireOp",EDGE,"E67.top")]}),1.0]])],"derivedFrom":subQ40})])]})]}),makeQuery(id+"F9.opExtrude","SWEPT_FACE",FACE,{"disambiguationData":[OSD([subQ7]),TDD([makeQuery(id+"F8.imprint","IMPRINT",EDGE,{"disambiguationData":[TD([[makeQuery(id+"F8.imprint","INTERSECT",VERTEX,{"derivedFrom":[subQ36,subQ34]}),-1.0]])],"derivedFrom":subQ36}),makeQuery(id+"F8.imprint","IMPRINT",EDGE,{"disambiguationData":[TD([[makeQuery(id+"F8.imprint","INTERSECT",VERTEX,{"derivedFrom":[subQ35,subQ28]}),1.0]])],"derivedFrom":subQ35})])]})]})});}
            var sketch = newSketch(context, id + "F17", { "sketchPlane" : qUnion([Q0])});
            skPoint(sketch, "E97.oppositeSnap0", {"position": v(60.33, 21.24) * mm});
            skPoint(sketch, "E97.oppositeSnap1", {"position": v(22.42, 47.6) * mm});
            skLineSegment(sketch, "E97.bottom", {"start": v(-22.4, 47.6) * mm, "end": v(22.42, 47.6) * mm});
            skLineSegment(sketch, "E97.top", {"start": v(-22.4, 21.24) * mm, "end": v(22.42, 21.24) * mm});
            skLineSegment(sketch, "E97.left", {"start": v(-22.4, 47.6) * mm, "end": v(-22.4, 21.24) * mm});
            skLineSegment(sketch, "E97.right", {"start": v(22.42, 47.6) * mm, "end": v(22.42, 21.24) * mm});
            skSolve(sketch);
        }
        {
            var Q0;
            Q0 = qSketchRegion(id + "F17", true);
            var Q1;
            Q1=makeQuery(id+"F3.opExtrude","CAP_FACE",FACE,{"disambiguationData":[OSD([sQuery(id+"F2.wireOp",EDGE,"E26.MirrorCS"),sQuery(id+"F2.wireOp",EDGE,"E27.MirrorCS"),sQuery(id+"F2.wireOp",EDGE,"E28.MirrorCS"),sQuery(id+"F2.wireOp",EDGE,"E25.MirrorCS")])],"isStart":false});
            extrude(context, id + "F18", {"entities" : qUnion([Q0, Q1]), "operationType" : NewBodyOperationType.REMOVE, "oppositeDirection" : true, "depth" : 25.4 * mm});
        }
        {
            var Q0;
            Q0=makeQuery(id+"F18.boolean.opBoolean","COPY",FACE,{"derivedFrom":makeQuery(id+"F18.opExtrude","SWEPT_FACE",FACE,{"disambiguationData":[OSD([sQuery(id+"F17.wireOp",EDGE,"E97.top")])]})});
            var sketch = newSketch(context, id + "F19", { "sketchPlane" : qUnion([Q0])});
            skLineSegment(sketch, "E98.bottom", {"start": v(-2.53, -58.1) * mm, "end": v(2.55, -58.1) * mm});
            skLineSegment(sketch, "E98.top", {"start": v(-2.53, -59.37) * mm, "end": v(2.55, -59.37) * mm});
            skLineSegment(sketch, "E98.left", {"start": v(-2.53, -58.1) * mm, "end": v(-2.53, -59.37) * mm});
            skLineSegment(sketch, "E98.right", {"start": v(2.55, -58.1) * mm, "end": v(2.55, -59.37) * mm});
            skSolve(sketch);
        }
        {
            var Q0;
            Q0=makeQuery(id+"F19.imprint","IMPRINT",FACE,{"disambiguationData":[TD([[makeQuery(id+"F19.imprint","IMPRINT",EDGE,{"derivedFrom":sQuery(id+"F19.wireOp",EDGE,"E98.bottom")}),-1.0]])]});
            extrude(context, id + "F20", {"entities" : qUnion([Q0]), "operationType" : NewBodyOperationType.REMOVE, "oppositeDirection" : true, "depth" : 2.54 * mm});
        }
        {
            var Q0;
            Q0=makeQuery(id+"F18.boolean.opBoolean","COPY",FACE,{"derivedFrom":makeQuery(id+"F18.opExtrude","SWEPT_FACE",FACE,{"disambiguationData":[OSD([sQuery(id+"F17.wireOp",EDGE,"E97.left")])]})});
            var sketch = newSketch(context, id + "F21", { "sketchPlane" : qUnion([Q0])});
            skLineSegment(sketch, "E99.bottom", {"start": v(-58.1, 36.95) * mm, "end": v(-59.37, 36.95) * mm});
            skLineSegment(sketch, "E99.top", {"start": v(-58.1, 31.87) * mm, "end": v(-59.37, 31.87) * mm});
            skLineSegment(sketch, "E99.left", {"start": v(-58.1, 36.95) * mm, "end": v(-58.1, 31.87) * mm});
            skLineSegment(sketch, "E99.right", {"start": v(-59.37, 36.95) * mm, "end": v(-59.37, 31.87) * mm});
            skSolve(sketch);
        }
        {
            var Q0;
            Q0=makeQuery(id+"F21.imprint","IMPRINT",FACE,{"disambiguationData":[TD([[makeQuery(id+"F21.imprint","IMPRINT",EDGE,{"derivedFrom":sQuery(id+"F21.wireOp",EDGE,"E99.bottom")}),1.0]])]});
            extrude(context, id + "F22", {"entities" : qUnion([Q0]), "operationType" : NewBodyOperationType.REMOVE, "oppositeDirection" : true, "depth" : 2.54 * mm});
        }
        {
            var Q0;
            Q0=makeQuery(id+"F18.boolean.opBoolean","COPY",FACE,{"derivedFrom":makeQuery(id+"F18.opExtrude","SWEPT_FACE",FACE,{"disambiguationData":[OSD([sQuery(id+"F17.wireOp",EDGE,"E97.right")])]})});
            var sketch = newSketch(context, id + "F23", { "sketchPlane" : qUnion([Q0])});
            skLineSegment(sketch, "E100.bottom", {"start": v(58.1, 36.96) * mm, "end": v(59.37, 36.96) * mm});
            skLineSegment(sketch, "E100.top", {"start": v(58.1, 31.88) * mm, "end": v(59.37, 31.88) * mm});
            skLineSegment(sketch, "E100.left", {"start": v(58.1, 36.96) * mm, "end": v(58.1, 31.88) * mm});
            skLineSegment(sketch, "E100.right", {"start": v(59.37, 36.96) * mm, "end": v(59.37, 31.88) * mm});
            skLineSegment(sketch, "E101", {"start": v(58.1, 36.96) * mm, "end": v(58.1, 47.6) * mm});
            skLineSegment(sketch, "E102", {"start": v(58.1, 31.88) * mm, "end": v(58.1, 21.24) * mm});
            skLineSegment(sketch, "E103", {"start": v(59.37, 36.96) * mm, "end": v(60.33, 36.96) * mm});
            skLineSegment(sketch, "E104", {"start": v(58.1, 36.96) * mm, "end": v(57.15, 36.96) * mm});
            skSolve(sketch);
        }
        {
            var Q0;
            Q0 = qSketchRegion(id + "F23", true);
            extrude(context, id + "F24", {"entities" : qUnion([Q0]), "operationType" : NewBodyOperationType.REMOVE, "oppositeDirection" : true, "depth" : 2.54 * mm});
        }
        {
            var Q0;
            Q0=makeQuery(id+"F3.opExtrude","CAP_EDGE",EDGE,{"disambiguationData":[OSD([sQuery(id+"F2.wireOp",EDGE,"E21.MirrorCS")])],"isStart":false});
            var Q1;
            Q1=makeQuery(id+"F3.opExtrude","CAP_EDGE",EDGE,{"disambiguationData":[OSD([sQuery(id+"F2.wireOp",EDGE,"E22.MirrorCS")])],"isStart":false});
            var Q2;
            Q2=makeQuery(id+"F3.opExtrude","CAP_EDGE",EDGE,{"disambiguationData":[OSD([sQuery(id+"F2.wireOp",EDGE,"E5")])],"isStart":false});
            var Q3;
            Q3=makeQuery(id+"F3.opExtrude","CAP_EDGE",EDGE,{"disambiguationData":[OSD([sQuery(id+"F2.wireOp",EDGE,"E6")])],"isStart":false});
            var Q4;
            Q4=makeQuery(id+"F3.opExtrude","CAP_EDGE",EDGE,{"disambiguationData":[OSD([sQuery(id+"F2.wireOp",EDGE,"E7")])],"isStart":false});
            var Q5;
            Q5=makeQuery(id+"F3.opExtrude","CAP_EDGE",EDGE,{"disambiguationData":[OSD([sQuery(id+"F2.wireOp",EDGE,"E9")])],"isStart":false});
            var Q6;
            Q6=makeQuery(id+"F3.opExtrude","CAP_EDGE",EDGE,{"disambiguationData":[OSD([sQuery(id+"F2.wireOp",EDGE,"E12")])],"isStart":false});
            var Q7;
            Q7=makeQuery(id+"F3.opExtrude","CAP_EDGE",EDGE,{"disambiguationData":[OSD([sQuery(id+"F2.wireOp",EDGE,"E10")])],"isStart":false});
            var Q8;
            Q8=makeQuery(id+"F3.opExtrude","CAP_EDGE",EDGE,{"disambiguationData":[OSD([sQuery(id+"F2.wireOp",EDGE,"E29.MirrorCS")])],"isStart":false});
            var Q9;
            Q9=makeQuery(id+"F3.opExtrude","CAP_EDGE",EDGE,{"disambiguationData":[OSD([sQuery(id+"F2.wireOp",EDGE,"E30.MirrorCS")])],"isStart":false});
            var Q10;
            Q10=makeQuery(id+"F3.opExtrude","CAP_EDGE",EDGE,{"disambiguationData":[OSD([sQuery(id+"F2.wireOp",EDGE,"E18")])],"isStart":false});
            var Q11;
            Q11=makeQuery(id+"F3.opExtrude","CAP_EDGE",EDGE,{"disambiguationData":[OSD([sQuery(id+"F2.wireOp",EDGE,"E17")])],"isStart":false});
            var Q12;
            Q12=makeQuery(id+"F3.opExtrude","CAP_EDGE",EDGE,{"disambiguationData":[OSD([sQuery(id+"F2.wireOp",EDGE,"E15")])],"isStart":false});
            var Q13;
            Q13=makeQuery(id+"F3.opExtrude","CAP_EDGE",EDGE,{"disambiguationData":[OSD([sQuery(id+"F2.wireOp",EDGE,"E14")])],"isStart":false});
            var Q14;
            Q14=makeQuery(id+"F3.opExtrude","CAP_EDGE",EDGE,{"disambiguationData":[OSD([sQuery(id+"F2.wireOp",EDGE,"E13")])],"isStart":false});
            var Q15;
            Q15=makeQuery(id+"F3.opExtrude","CAP_EDGE",EDGE,{"disambiguationData":[OSD([sQuery(id+"F2.wireOp",EDGE,"E16")])],"isStart":false});
            var Q16;
            Q16=makeQuery(id+"F3.opExtrude","CAP_EDGE",EDGE,{"disambiguationData":[OSD([sQuery(id+"F2.wireOp",EDGE,"E4")])],"isStart":false});
            var Q17;
            Q17=makeQuery(id+"F3.opExtrude","CAP_EDGE",EDGE,{"disambiguationData":[OSD([sQuery(id+"F2.wireOp",EDGE,"E3")])],"isStart":false});
            var Q18;
            Q18=makeQuery(id+"F3.opExtrude","CAP_EDGE",EDGE,{"disambiguationData":[OSD([sQuery(id+"F2.wireOp",EDGE,"E2")])],"isStart":false});
            var Q19;
            {var subQ0=sQuery(id+"F6.wireOp",EDGE,"E67.right");var subQ1=sQuery(id+"F6.wireOp",EDGE,"E67.top");Q19=makeQuery(id+"F12.boolean.opBoolean","SPLIT",EDGE,{"disambiguationData":[TD([makeQuery(id+"F7.opExtrude","SWEPT_FACE",FACE,{"disambiguationData":[OSD([subQ1])]})])],"derivedFrom":makeQuery(id+"F7.opExtrude","CAP_EDGE",EDGE,{"disambiguationData":[OSD([subQ0])],"isStart":false})});}
            var Q20;
            Q20=makeQuery(id+"F7.opExtrude","CAP_EDGE",EDGE,{"disambiguationData":[OSD([sQuery(id+"F6.wireOp",EDGE,"E67.top")])],"isStart":false});
            var Q21;
            Q21=makeQuery(id+"F7.opExtrude","CAP_EDGE",EDGE,{"disambiguationData":[OSD([sQuery(id+"F6.wireOp",EDGE,"E69.bottom")])],"isStart":false});
            var Q22;
            Q22=makeQuery(id+"F7.opExtrude","CAP_EDGE",EDGE,{"disambiguationData":[OSD([sQuery(id+"F6.wireOp",EDGE,"E69.right")])],"isStart":false});
            var Q23;
            Q23=makeQuery(id+"F7.opExtrude","CAP_EDGE",EDGE,{"disambiguationData":[OSD([sQuery(id+"F6.wireOp",EDGE,"E69.top")])],"isStart":false});
            var Q24;
            Q24=makeQuery(id+"F7.opExtrude","CAP_EDGE",EDGE,{"disambiguationData":[OSD([sQuery(id+"F6.wireOp",EDGE,"E72.top")])],"isStart":false});
            var Q25;
            Q25=makeQuery(id+"F7.opExtrude","CAP_EDGE",EDGE,{"disambiguationData":[OSD([sQuery(id+"F6.wireOp",EDGE,"E72.right")])],"isStart":false});
            var Q26;
            Q26=makeQuery(id+"F7.opExtrude","CAP_EDGE",EDGE,{"disambiguationData":[OSD([sQuery(id+"F6.wireOp",EDGE,"E72.bottom")])],"isStart":false});
            var Q27;
            Q27=makeQuery(id+"F7.opExtrude","CAP_EDGE",EDGE,{"disambiguationData":[OSD([sQuery(id+"F6.wireOp",EDGE,"E73.bottom")])],"isStart":false});
            var Q28;
            Q28=makeQuery(id+"F7.opExtrude","CAP_EDGE",EDGE,{"disambiguationData":[OSD([sQuery(id+"F6.wireOp",EDGE,"E73.right")])],"isStart":false});
            var Q29;
            Q29=makeQuery(id+"F7.opExtrude","CAP_EDGE",EDGE,{"disambiguationData":[OSD([sQuery(id+"F6.wireOp",EDGE,"E73.top")])],"isStart":false});
            var Q30;
            Q30=makeQuery(id+"F7.opExtrude","CAP_EDGE",EDGE,{"disambiguationData":[OSD([sQuery(id+"F6.wireOp",EDGE,"E71.top")])],"isStart":false});
            var Q31;
            Q31=makeQuery(id+"F7.opExtrude","CAP_EDGE",EDGE,{"disambiguationData":[OSD([sQuery(id+"F6.wireOp",EDGE,"E71.left")])],"isStart":false});
            var Q32;
            Q32=makeQuery(id+"F7.opExtrude","CAP_EDGE",EDGE,{"disambiguationData":[OSD([sQuery(id+"F6.wireOp",EDGE,"E71.bottom")])],"isStart":false});
            var Q33;
            Q33=makeQuery(id+"F7.opExtrude","CAP_EDGE",EDGE,{"disambiguationData":[OSD([sQuery(id+"F6.wireOp",EDGE,"E70.bottom")])],"isStart":false});
            var Q34;
            Q34=makeQuery(id+"F7.opExtrude","CAP_EDGE",EDGE,{"disambiguationData":[OSD([sQuery(id+"F6.wireOp",EDGE,"E70.right")])],"isStart":false});
            var Q35;
            Q35=makeQuery(id+"F7.opExtrude","CAP_EDGE",EDGE,{"disambiguationData":[OSD([sQuery(id+"F6.wireOp",EDGE,"E70.top")])],"isStart":false});
            var Q36;
            Q36=makeQuery(id+"F7.opExtrude","CAP_EDGE",EDGE,{"disambiguationData":[OSD([sQuery(id+"F6.wireOp",EDGE,"E70.left")])],"isStart":false});
            var Q37;
            Q37=makeQuery(id+"F7.opExtrude","CAP_EDGE",EDGE,{"disambiguationData":[OSD([sQuery(id+"F6.wireOp",EDGE,"E68.top")])],"isStart":false});
            var Q38;
            {var subQ0=sQuery(id+"F6.wireOp",EDGE,"E68.right");var subQ1=sQuery(id+"F6.wireOp",EDGE,"E68.top");Q38=makeQuery(id+"F12.boolean.opBoolean","SPLIT",EDGE,{"disambiguationData":[TD([makeQuery(id+"F7.opExtrude","SWEPT_FACE",FACE,{"disambiguationData":[OSD([subQ1])]})])],"derivedFrom":makeQuery(id+"F7.opExtrude","CAP_EDGE",EDGE,{"disambiguationData":[OSD([subQ0])],"isStart":false})});}
            var Q39;
            Q39=makeQuery(id+"F5.opExtrude","CAP_EDGE",EDGE,{"disambiguationData":[OSD([sQuery(id+"F4.wireOp",EDGE,"E54.MirrorCS")])],"isStart":false});
            var Q40;
            Q40=makeQuery(id+"F5.opExtrude","CAP_EDGE",EDGE,{"disambiguationData":[OSD([sQuery(id+"F4.wireOp",EDGE,"E55.MirrorCS")])],"isStart":false});
            var Q41;
            Q41=makeQuery(id+"F5.opExtrude","CAP_EDGE",EDGE,{"disambiguationData":[OSD([sQuery(id+"F4.wireOp",EDGE,"E38")])],"isStart":false});
            var Q42;
            Q42=makeQuery(id+"F5.opExtrude","CAP_EDGE",EDGE,{"disambiguationData":[OSD([sQuery(id+"F4.wireOp",EDGE,"E39")])],"isStart":false});
            var Q43;
            Q43=makeQuery(id+"F5.opExtrude","CAP_EDGE",EDGE,{"disambiguationData":[OSD([sQuery(id+"F4.wireOp",EDGE,"E40")])],"isStart":false});
            var Q44;
            Q44=makeQuery(id+"F5.opExtrude","CAP_EDGE",EDGE,{"disambiguationData":[OSD([sQuery(id+"F4.wireOp",EDGE,"E35")])],"isStart":false});
            var Q45;
            Q45=makeQuery(id+"F5.opExtrude","CAP_EDGE",EDGE,{"disambiguationData":[OSD([sQuery(id+"F4.wireOp",EDGE,"E37")])],"isStart":false});
            var Q46;
            Q46=makeQuery(id+"F5.opExtrude","CAP_EDGE",EDGE,{"disambiguationData":[OSD([sQuery(id+"F4.wireOp",EDGE,"E36")])],"isStart":false});
            var Q47;
            Q47=makeQuery(id+"F5.opExtrude","CAP_EDGE",EDGE,{"disambiguationData":[OSD([sQuery(id+"F4.wireOp",EDGE,"E46")])],"isStart":false});
            var Q48;
            Q48=makeQuery(id+"F5.opExtrude","CAP_EDGE",EDGE,{"disambiguationData":[OSD([sQuery(id+"F4.wireOp",EDGE,"E47")])],"isStart":false});
            var Q49;
            Q49=makeQuery(id+"F5.opExtrude","CAP_EDGE",EDGE,{"disambiguationData":[OSD([sQuery(id+"F4.wireOp",EDGE,"E48")])],"isStart":false});
            var Q50;
            Q50=makeQuery(id+"F5.opExtrude","CAP_EDGE",EDGE,{"disambiguationData":[OSD([sQuery(id+"F0.wireOp",EDGE,"E0.top")])],"isStart":false});
            var Q51;
            Q51=makeQuery(id+"F5.opExtrude","CAP_EDGE",EDGE,{"disambiguationData":[OSD([sQuery(id+"F4.wireOp",EDGE,"E50")])],"isStart":false});
            var Q52;
            Q52=makeQuery(id+"F5.opExtrude","CAP_EDGE",EDGE,{"disambiguationData":[OSD([sQuery(id+"F4.wireOp",EDGE,"E53")])],"isStart":false});
            var Q53;
            Q53=makeQuery(id+"F5.opExtrude","CAP_EDGE",EDGE,{"disambiguationData":[OSD([sQuery(id+"F4.wireOp",EDGE,"E51")])],"isStart":false});
            var Q54;
            Q54=makeQuery(id+"F5.opExtrude","CAP_EDGE",EDGE,{"disambiguationData":[OSD([sQuery(id+"F4.wireOp",EDGE,"E43")])],"isStart":false});
            var Q55;
            Q55=makeQuery(id+"F5.opExtrude","CAP_EDGE",EDGE,{"disambiguationData":[OSD([sQuery(id+"F4.wireOp",EDGE,"E42")])],"isStart":false});
            var Q56;
            Q56=makeQuery(id+"F5.opExtrude","CAP_EDGE",EDGE,{"disambiguationData":[OSD([sQuery(id+"F4.wireOp",EDGE,"E45")])],"isStart":false});
            var Q57;
            Q57=makeQuery(id+"F5.opExtrude","CAP_EDGE",EDGE,{"disambiguationData":[OSD([sQuery(id+"F4.wireOp",EDGE,"E58.MirrorCS")])],"isStart":false});
            var Q58;
            Q58=makeQuery(id+"F5.opExtrude","CAP_EDGE",EDGE,{"disambiguationData":[OSD([sQuery(id+"F4.wireOp",EDGE,"E61.MirrorCS")])],"isStart":false});
            var Q59;
            Q59=makeQuery(id+"F5.opExtrude","CAP_EDGE",EDGE,{"disambiguationData":[OSD([sQuery(id+"F4.wireOp",EDGE,"E59.MirrorCS")])],"isStart":false});
            var Q60;
            Q60=makeQuery(id+"F5.opExtrude","CAP_EDGE",EDGE,{"disambiguationData":[OSD([sQuery(id+"F4.wireOp",EDGE,"E63.MirrorCS")])],"isStart":false});
            var Q61;
            Q61=makeQuery(id+"F5.opExtrude","CAP_EDGE",EDGE,{"disambiguationData":[OSD([sQuery(id+"F4.wireOp",EDGE,"E62.MirrorCS")])],"isStart":false});
            var Q62;
            Q62=makeQuery(id+"F5.opExtrude","CAP_EDGE",EDGE,{"disambiguationData":[OSD([sQuery(id+"F4.wireOp",EDGE,"E65.MirrorCS")])],"isStart":false});
            var Q63;
            {var subQ1=sQuery(id+"F0.wireOp",EDGE,"E0.right");var subQ2=sQuery(id+"F0.wireOp",EDGE,"E0.top");var subQ3=makeQuery(id+"F1.opExtrude","SWEPT_EDGE",EDGE,{"disambiguationData":[OSD([subQ2,subQ1])]});Q63=makeQuery(id+"F9.opExtrude","CAP_EDGE",EDGE,{"disambiguationData":[OSD([subQ2,subQ1]),TDD([makeQuery(id+"F8.imprint","IMPRINT",EDGE,{"disambiguationData":[TD([[makeQuery(id+"F8.imprint","INTERSECT",VERTEX,{"derivedFrom":[subQ3,sQuery(id+"F8.wireOp",EDGE,"E79.right")]}),-1.0]])],"derivedFrom":subQ3})])],"isStart":false});}
            var Q64;
            Q64=makeQuery(id+"F9.opExtrude","CAP_EDGE",EDGE,{"disambiguationData":[OSD([sQuery(id+"F8.wireOp",EDGE,"E79.top")])],"isStart":false});
            var Q65;
            Q65=makeQuery(id+"F9.opExtrude","CAP_EDGE",EDGE,{"disambiguationData":[OSD([sQuery(id+"F8.wireOp",EDGE,"E79.right")])],"isStart":false});
            var Q66;
            Q66=makeQuery(id+"F9.opExtrude","CAP_EDGE",EDGE,{"disambiguationData":[OSD([sQuery(id+"F8.wireOp",EDGE,"E80.top")])],"isStart":false});
            var Q67;
            Q67=makeQuery(id+"F9.opExtrude","CAP_EDGE",EDGE,{"disambiguationData":[OSD([sQuery(id+"F8.wireOp",EDGE,"E80.right")])],"isStart":false});
            var Q68;
            {var subQ1=sQuery(id+"F0.wireOp",EDGE,"E0.right");var subQ2=sQuery(id+"F0.wireOp",EDGE,"E0.top");var subQ3=makeQuery(id+"F1.opExtrude","SWEPT_EDGE",EDGE,{"disambiguationData":[OSD([subQ2,subQ1])]});Q68=makeQuery(id+"F9.opExtrude","CAP_EDGE",EDGE,{"disambiguationData":[OSD([subQ2,subQ1]),TDD([makeQuery(id+"F8.imprint","IMPRINT",EDGE,{"disambiguationData":[TD([[makeQuery(id+"F8.imprint","INTERSECT",VERTEX,{"derivedFrom":[subQ3,sQuery(id+"F8.wireOp",EDGE,"E80.right")]}),1.0]])],"derivedFrom":subQ3})])],"isStart":false});}
            var Q69;
            Q69=makeQuery(id+"F9.opExtrude","CAP_EDGE",EDGE,{"disambiguationData":[OSD([sQuery(id+"F8.wireOp",EDGE,"E78.top")])],"isStart":false});
            var Q70;
            Q70=makeQuery(id+"F9.opExtrude","CAP_EDGE",EDGE,{"disambiguationData":[OSD([sQuery(id+"F8.wireOp",EDGE,"E78.left")])],"isStart":false});
            var Q71;
            Q71=makeQuery(id+"F9.opExtrude","CAP_EDGE",EDGE,{"disambiguationData":[OSD([sQuery(id+"F8.wireOp",EDGE,"E78.bottom")])],"isStart":false});
            var Q72;
            Q72=makeQuery(id+"F9.opExtrude","CAP_EDGE",EDGE,{"disambiguationData":[OSD([sQuery(id+"F8.wireOp",EDGE,"E77.bottom")])],"isStart":false});
            var Q73;
            Q73=makeQuery(id+"F9.opExtrude","CAP_EDGE",EDGE,{"disambiguationData":[OSD([sQuery(id+"F8.wireOp",EDGE,"E77.right")])],"isStart":false});
            var Q74;
            Q74=makeQuery(id+"F9.opExtrude","CAP_EDGE",EDGE,{"disambiguationData":[OSD([sQuery(id+"F8.wireOp",EDGE,"E77.top")])],"isStart":false});
            var Q75;
            Q75=makeQuery(id+"F9.opExtrude","CAP_EDGE",EDGE,{"disambiguationData":[OSD([sQuery(id+"F8.wireOp",EDGE,"E77.left")])],"isStart":false});
            var Q76;
            Q76=makeQuery(id+"F9.opExtrude","CAP_EDGE",EDGE,{"disambiguationData":[OSD([sQuery(id+"F8.wireOp",EDGE,"E76.right")])],"isStart":false});
            var Q77;
            Q77=makeQuery(id+"F9.opExtrude","CAP_EDGE",EDGE,{"disambiguationData":[OSD([sQuery(id+"F8.wireOp",EDGE,"E76.bottom")])],"isStart":false});
            var Q78;
            Q78=makeQuery(id+"F9.opExtrude","CAP_EDGE",EDGE,{"disambiguationData":[OSD([sQuery(id+"F8.wireOp",EDGE,"E76.top")])],"isStart":false});
            var Q79;
            Q79=makeQuery(id+"F9.opExtrude","CAP_EDGE",EDGE,{"disambiguationData":[OSD([sQuery(id+"F8.wireOp",EDGE,"E74.top")])],"isStart":false});
            var Q80;
            Q80=makeQuery(id+"F9.opExtrude","CAP_EDGE",EDGE,{"disambiguationData":[OSD([sQuery(id+"F8.wireOp",EDGE,"E74.right")])],"isStart":false});
            var Q81;
            Q81=makeQuery(id+"F9.opExtrude","CAP_EDGE",EDGE,{"disambiguationData":[OSD([sQuery(id+"F8.wireOp",EDGE,"E75.right")])],"isStart":false});
            var Q82;
            Q82=makeQuery(id+"F9.opExtrude","CAP_EDGE",EDGE,{"disambiguationData":[OSD([sQuery(id+"F8.wireOp",EDGE,"E75.top")])],"isStart":false});
            var Q83;
            Q83=makeQuery(id+"F3.opExtrude","CAP_EDGE",EDGE,{"disambiguationData":[OSD([sQuery(id+"F2.wireOp",EDGE,"E20")])],"isStart":false});
            chamfer(context, id + "F25", {"entities" : qUnion([Q0, Q1, Q2, Q3, Q4, Q5, Q6, Q7, Q8, Q9, Q10, Q11, Q12, Q13, Q14, Q15, Q16, Q17, Q18, Q19, Q20, Q21, Q22, Q23, Q24, Q25, Q26, Q27, Q28, Q29, Q30, Q31, Q32, Q33, Q34, Q35, Q36, Q37, Q38, Q39, Q40, Q41, Q42, Q43, Q44, Q45, Q46, Q47, Q48, Q49, Q50, Q51, Q52, Q53, Q54, Q55, Q56, Q57, Q58, Q59, Q60, Q61, Q62, Q63, Q64, Q65, Q66, Q67, Q68, Q69, Q70, Q71, Q72, Q73, Q74, Q75, Q76, Q77, Q78, Q79, Q80, Q81, Q82, Q83]), "width" : 1.27 * mm, "tangentPropagation" : true});
        }
        {
            var Q0;
            Q0=makeQuery(id+"F3.opExtrude","CAP_EDGE",EDGE,{"disambiguationData":[OSD([sQuery(id+"F2.wireOp",EDGE,"E24.MirrorCS")])],"isStart":false});
            var Q1;
            Q1=makeQuery(id+"F3.opExtrude","CAP_EDGE",EDGE,{"disambiguationData":[OSD([sQuery(id+"F2.wireOp",EDGE,"E8")])],"isStart":false});
            var Q2;
            Q2=makeQuery(id+"F3.opExtrude","CAP_EDGE",EDGE,{"disambiguationData":[OSD([sQuery(id+"F2.wireOp",EDGE,"E1")])],"isStart":false});
            var Q3;
            Q3=makeQuery(id+"F3.opExtrude","CAP_EDGE",EDGE,{"disambiguationData":[OSD([sQuery(id+"F2.wireOp",EDGE,"E32.MirrorCS")])],"isStart":false});
            var Q4;
            Q4=makeQuery(id+"F3.opExtrude","CAP_EDGE",EDGE,{"disambiguationData":[OSD([sQuery(id+"F2.wireOp",EDGE,"E11")])],"isStart":false});
            var Q5;
            Q5=makeQuery(id+"F3.opExtrude","CAP_EDGE",EDGE,{"disambiguationData":[OSD([sQuery(id+"F2.wireOp",EDGE,"E19")])],"isStart":false});
            var Q6;
            Q6=makeQuery(id+"F5.opExtrude","CAP_EDGE",EDGE,{"disambiguationData":[OSD([sQuery(id+"F4.wireOp",EDGE,"E57.MirrorCS")])],"isStart":false});
            var Q7;
            Q7=makeQuery(id+"F5.opExtrude","CAP_EDGE",EDGE,{"disambiguationData":[OSD([sQuery(id+"F4.wireOp",EDGE,"E41")])],"isStart":false});
            var Q8;
            Q8=makeQuery(id+"F5.opExtrude","CAP_EDGE",EDGE,{"disambiguationData":[OSD([sQuery(id+"F4.wireOp",EDGE,"E34")])],"isStart":false});
            var Q9;
            Q9=makeQuery(id+"F5.opExtrude","CAP_EDGE",EDGE,{"disambiguationData":[OSD([sQuery(id+"F4.wireOp",EDGE,"E44")])],"isStart":false});
            var Q10;
            Q10=makeQuery(id+"F5.opExtrude","CAP_EDGE",EDGE,{"disambiguationData":[OSD([sQuery(id+"F4.wireOp",EDGE,"E52")])],"isStart":false});
            chamfer(context, id + "F26", {"entities" : qUnion([Q0, Q1, Q2, Q3, Q4, Q5, Q6, Q7, Q8, Q9, Q10]), "width" : 1.27 * mm, "tangentPropagation" : true});
        }
        {
            var Q0;
            Q0=makeQuery(id+"F5.opExtrude","CAP_FACE",FACE,{"disambiguationData":[OSD([sQuery(id+"F4.wireOp",EDGE,"E59.MirrorCS"),sQuery(id+"F4.wireOp",EDGE,"E60.MirrorCS"),sQuery(id+"F4.wireOp",EDGE,"E61.MirrorCS"),sQuery(id+"F4.wireOp",EDGE,"E58.MirrorCS")])],"isStart":false});
            var sketch = newSketch(context, id + "F27", { "sketchPlane" : qUnion([Q0])});
            skLineSegment(sketch, "E105.bottom", {"start": v(-6.36, 41.24) * mm, "end": v(6.34, 41.24) * mm});
            skLineSegment(sketch, "E105.top", {"start": v(-6.36, 47.6) * mm, "end": v(6.34, 47.6) * mm});
            skLineSegment(sketch, "E105.left", {"start": v(-6.36, 41.24) * mm, "end": v(-6.36, 47.6) * mm});
            skLineSegment(sketch, "E105.right", {"start": v(6.34, 41.24) * mm, "end": v(6.34, 47.6) * mm});
            skSolve(sketch);
        }
        {
            var Q0;
            Q0 = qSketchRegion(id + "F27", true);
            extrude(context, id + "F28", {"entities" : qUnion([Q0]), "operationType" : NewBodyOperationType.ADD, "depth" : 0.64 * mm});
        }
        {
            var Q0;
            Q0=makeQuery(id+"F28.opExtrude","CAP_FACE",FACE,{"disambiguationData":[OSD([sQuery(id+"F27.wireOp",EDGE,"E105.bottom"),sQuery(id+"F27.wireOp",EDGE,"E105.top"),sQuery(id+"F27.wireOp",EDGE,"E105.left"),sQuery(id+"F27.wireOp",EDGE,"E105.right")])],"isStart":false});
            var sketch = newSketch(context, id + "F29", { "sketchPlane" : qUnion([Q0])});
            skLineSegment(sketch, "E106.bottom", {"start": v(-4.45, 45.69) * mm, "end": v(4.44, 45.69) * mm});
            skLineSegment(sketch, "E106.top", {"start": v(-4.45, 49.5) * mm, "end": v(4.44, 49.5) * mm});
            skLineSegment(sketch, "E106.left", {"start": v(-4.45, 45.69) * mm, "end": v(-4.45, 49.5) * mm});
            skLineSegment(sketch, "E106.right", {"start": v(4.44, 45.69) * mm, "end": v(4.44, 49.5) * mm});
            skSolve(sketch);
        }
        {
            var Q0;
            Q0 = qSketchRegion(id + "F29", true);
            extrude(context, id + "F30", {"entities" : qUnion([Q0]), "operationType" : NewBodyOperationType.ADD, "depth" : 3.8 * mm});
        }
        {
            var Q0;
            Q0=makeQuery(id+"F30.opExtrude","CAP_EDGE",EDGE,{"disambiguationData":[OSD([sQuery(id+"F29.wireOp",EDGE,"E106.top")])],"isStart":false});
            var Q1;
            Q1=makeQuery(id+"F30.opExtrude","CAP_EDGE",EDGE,{"disambiguationData":[OSD([sQuery(id+"F29.wireOp",EDGE,"E106.bottom")])],"isStart":false});
            fillet(context, id + "F31", {"entities" : qUnion([Q0, Q1]), "radius" : 1.9 * mm, "tangentPropagation" : true, "allowEdgeOverflow" : false});
        }
        {
            var Q0;
            Q0=makeQuery(id+"F5.opExtrude","CAP_FACE",FACE,{"disambiguationData":[OSD([sQuery(id+"F4.wireOp",EDGE,"E54.MirrorCS"),sQuery(id+"F4.wireOp",EDGE,"E55.MirrorCS"),sQuery(id+"F4.wireOp",EDGE,"E56.MirrorCS"),sQuery(id+"F4.wireOp",EDGE,"E57.MirrorCS")])],"isStart":false});
            var sketch = newSketch(context, id + "F32", { "sketchPlane" : qUnion([Q0])});
            skLineSegment(sketch, "E107.bottom", {"start": v(-38.49, 47.6) * mm, "end": v(-51.19, 47.6) * mm});
            skLineSegment(sketch, "E107.top", {"start": v(-38.49, 41.24) * mm, "end": v(-51.19, 41.24) * mm});
            skLineSegment(sketch, "E107.left", {"start": v(-38.49, 47.6) * mm, "end": v(-38.49, 41.24) * mm});
            skLineSegment(sketch, "E107.right", {"start": v(-51.19, 47.6) * mm, "end": v(-51.19, 41.24) * mm});
            skSolve(sketch);
        }
        {
            var Q0;
            Q0 = qSketchRegion(id + "F32", true);
            extrude(context, id + "F33", {"entities" : qUnion([Q0]), "operationType" : NewBodyOperationType.ADD, "depth" : 0.64 * mm});
        }
        {
            var Q0;
            Q0=makeQuery(id+"F5.opExtrude","CAP_FACE",FACE,{"disambiguationData":[OSD([sQuery(id+"F4.wireOp",EDGE,"E62.MirrorCS"),sQuery(id+"F4.wireOp",EDGE,"E63.MirrorCS"),sQuery(id+"F4.wireOp",EDGE,"E64.MirrorCS"),sQuery(id+"F4.wireOp",EDGE,"E65.MirrorCS")])],"isStart":false});
            var sketch = newSketch(context, id + "F34", { "sketchPlane" : qUnion([Q0])});
            skLineSegment(sketch, "E108.bottom", {"start": v(38.22, 47.6) * mm, "end": v(50.92, 47.6) * mm});
            skLineSegment(sketch, "E108.top", {"start": v(38.22, 41.24) * mm, "end": v(50.92, 41.24) * mm});
            skLineSegment(sketch, "E108.left", {"start": v(38.22, 47.6) * mm, "end": v(38.22, 41.24) * mm});
            skLineSegment(sketch, "E108.right", {"start": v(50.92, 47.6) * mm, "end": v(50.92, 41.24) * mm});
            skSolve(sketch);
        }
        {
            var Q0;
            Q0=makeQuery(id+"F34.imprint","IMPRINT",FACE,{"disambiguationData":[TD([[makeQuery(id+"F34.imprint","IMPRINT",EDGE,{"derivedFrom":sQuery(id+"F34.wireOp",EDGE,"E108.bottom")}),1.0]])]});
            extrude(context, id + "F35", {"entities" : qUnion([Q0]), "operationType" : NewBodyOperationType.ADD, "depth" : 0.64 * mm});
        }
        {
            var Q0;
            Q0=makeQuery(id+"F33.opExtrude","CAP_FACE",FACE,{"disambiguationData":[OSD([sQuery(id+"F32.wireOp",EDGE,"E107.bottom"),sQuery(id+"F32.wireOp",EDGE,"E107.top"),sQuery(id+"F32.wireOp",EDGE,"E107.left"),sQuery(id+"F32.wireOp",EDGE,"E107.right")])],"isStart":false});
            var sketch = newSketch(context, id + "F36", { "sketchPlane" : qUnion([Q0])});
            skLineSegment(sketch, "E109.bottom", {"start": v(-49.28, 45.69) * mm, "end": v(-40.4, 45.69) * mm});
            skLineSegment(sketch, "E109.top", {"start": v(-49.28, 49.5) * mm, "end": v(-40.4, 49.5) * mm});
            skLineSegment(sketch, "E109.left", {"start": v(-49.28, 45.69) * mm, "end": v(-49.28, 49.5) * mm});
            skLineSegment(sketch, "E109.right", {"start": v(-40.4, 45.69) * mm, "end": v(-40.4, 49.5) * mm});
            skSolve(sketch);
        }
        {
            var Q0;
            Q0=makeQuery(id+"F35.opExtrude","CAP_FACE",FACE,{"disambiguationData":[OSD([sQuery(id+"F34.wireOp",EDGE,"E108.bottom"),sQuery(id+"F34.wireOp",EDGE,"E108.top"),sQuery(id+"F34.wireOp",EDGE,"E108.left"),sQuery(id+"F34.wireOp",EDGE,"E108.right")])],"isStart":false});
            var sketch = newSketch(context, id + "F37", { "sketchPlane" : qUnion([Q0])});
            skLineSegment(sketch, "E110.bottom", {"start": v(40.13, 45.69) * mm, "end": v(49.02, 45.69) * mm});
            skLineSegment(sketch, "E110.top", {"start": v(40.13, 49.5) * mm, "end": v(49.02, 49.5) * mm});
            skLineSegment(sketch, "E110.left", {"start": v(40.13, 45.69) * mm, "end": v(40.13, 49.5) * mm});
            skLineSegment(sketch, "E110.right", {"start": v(49.02, 45.69) * mm, "end": v(49.02, 49.5) * mm});
            skSolve(sketch);
        }
        {
            var Q0;
            {var subQ0=sQuery(id+"F36.wireOp",EDGE,"E109.top");Q0=makeQuery(id+"F36.imprint","IMPRINT",FACE,{"disambiguationData":[TD([[makeQuery(id+"F36.imprint","IMPRINT",EDGE,{"derivedFrom":subQ0}),-1.0]])]});}
            var Q1;
            {var subQ0=sQuery(id+"F36.wireOp",EDGE,"E109.bottom");Q1=makeQuery(id+"F36.imprint","IMPRINT",FACE,{"disambiguationData":[TD([[makeQuery(id+"F36.imprint","IMPRINT",EDGE,{"derivedFrom":subQ0}),1.0]])]});}
            var Q2;
            {var subQ0=sQuery(id+"F37.wireOp",EDGE,"E110.top");Q2=makeQuery(id+"F37.imprint","IMPRINT",FACE,{"disambiguationData":[TD([[makeQuery(id+"F37.imprint","IMPRINT",EDGE,{"derivedFrom":subQ0}),-1.0]])]});}
            var Q3;
            {var subQ0=sQuery(id+"F37.wireOp",EDGE,"E110.bottom");Q3=makeQuery(id+"F37.imprint","IMPRINT",FACE,{"disambiguationData":[TD([[makeQuery(id+"F37.imprint","IMPRINT",EDGE,{"derivedFrom":subQ0}),1.0]])]});}
            extrude(context, id + "F38", {"entities" : qUnion([Q0, Q1, Q2, Q3]), "operationType" : NewBodyOperationType.ADD, "depth" : 3.8 * mm});
        }
        {
            var Q0;
            Q0=makeQuery(id+"F38.opExtrude","CAP_EDGE",EDGE,{"disambiguationData":[OSD([sQuery(id+"F36.wireOp",EDGE,"E109.top")])],"isStart":false});
            var Q1;
            Q1=makeQuery(id+"F38.opExtrude","CAP_EDGE",EDGE,{"disambiguationData":[OSD([sQuery(id+"F37.wireOp",EDGE,"E110.top")])],"isStart":false});
            var Q2;
            Q2=makeQuery(id+"F38.opExtrude","CAP_EDGE",EDGE,{"disambiguationData":[OSD([sQuery(id+"F37.wireOp",EDGE,"E110.bottom")])],"isStart":false});
            var Q3;
            Q3=makeQuery(id+"F38.opExtrude","CAP_EDGE",EDGE,{"disambiguationData":[OSD([sQuery(id+"F36.wireOp",EDGE,"E109.bottom")])],"isStart":false});
            fillet(context, id + "F39", {"entities" : qUnion([Q0, Q1, Q2, Q3]), "radius" : 1.9 * mm, "tangentPropagation" : true, "allowEdgeOverflow" : false});
        }
    });
